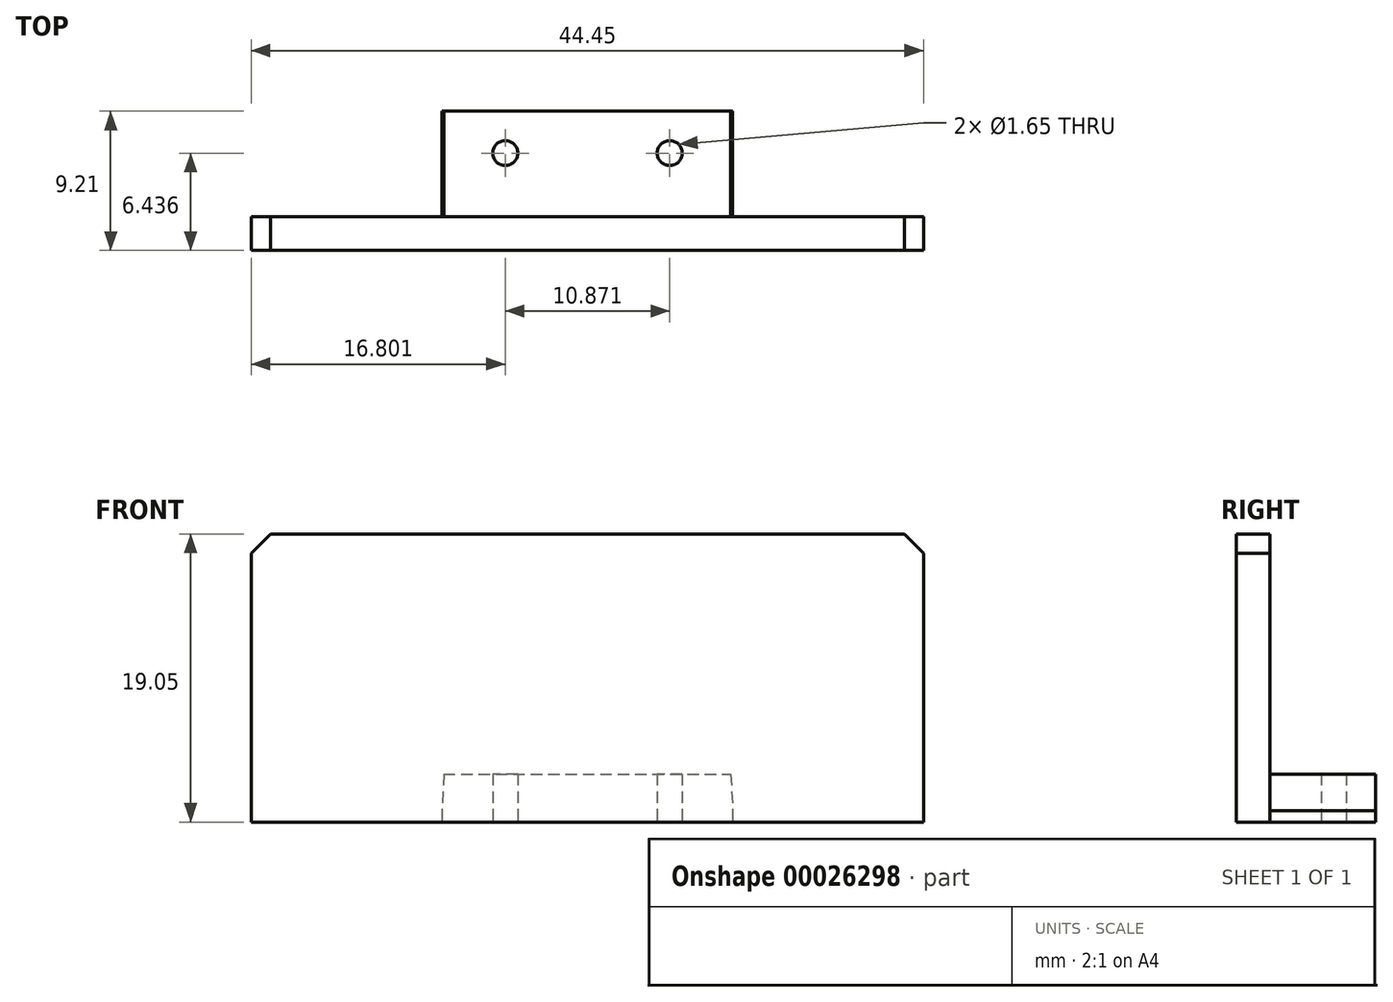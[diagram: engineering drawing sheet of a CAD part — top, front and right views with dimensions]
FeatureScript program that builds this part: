
annotation { "Feature Type Name" : "Feature", "Feature Type Description" : "" }
export const myFeature = defineFeature(function(context is Context, id is Id, definition is map)
    precondition{}
    {
        {
            var Q0;
            Q0=qCreatedBy(makeId("Top.planeOp"),FACE);
            var sketch = newSketch(context, id + "F0", { "sketchPlane" : qUnion([Q0])});
            skLineSegment(sketch, "E0.bottom", {"start": v(0, 0) * mm, "end": v(19.23, 0) * mm});
            skLineSegment(sketch, "E0.top", {"start": v(0, 6.99) * mm, "end": v(19.23, 6.99) * mm});
            skLineSegment(sketch, "E0.left", {"start": v(0, 0) * mm, "end": v(0, 6.99) * mm});
            skLineSegment(sketch, "E0.right", {"start": v(19.23, 0) * mm, "end": v(19.23, 6.99) * mm});
            skLineSegment(sketch, "E1", {"start": v(9.61, 6.99) * mm, "end": v(9.61, 0) * mm, "construction": true});
            skSolve(sketch);
        }
        {
            var Q0;
            Q0=makeQuery(id+"F0.imprint","IMPRINT",FACE,{"disambiguationData":[TD([[makeQuery(id+"F0.imprint","IMPRINT",EDGE,{"derivedFrom":sQuery(id+"F0.wireOp",EDGE,"E0.bottom")}),1.0]])]});
            extrude(context, id + "F1", {"entities" : qUnion([Q0]), "depth" : 3.17 * mm});
        }
        {
            var Q0;
            Q0=makeQuery(id+"F1.opExtrude","CAP_FACE",FACE,{"disambiguationData":[OSD([sQuery(id+"F0.wireOp",EDGE,"E0.bottom"),sQuery(id+"F0.wireOp",EDGE,"E0.top"),sQuery(id+"F0.wireOp",EDGE,"E0.left"),sQuery(id+"F0.wireOp",EDGE,"E0.right")])],"isStart":false});
            var sketch = newSketch(context, id + "F2", { "sketchPlane" : qUnion([Q0])});
            skCircle(sketch, "E2", {"center": v(4.2, 4.22) * mm, "radius": 1.71 * mm});
            skSolve(sketch);
        }
        {
            var Q0;
            Q0=makeQuery(id+"F2.imprint","IMPRINT",FACE,{"disambiguationData":[TD([[makeQuery(id+"F2.imprint","IMPRINT",EDGE,{"derivedFrom":sQuery(id+"F2.wireOp",EDGE,"E2")}),-1.0]])]});
            cPlane(context, id + "F3", {"entities" : qUnion([Q0]), "cplaneType" : CPlaneType.OFFSET, "offset" : 0.84 * mm, "width" : 152.4 * mm, "height" : 152.4 * mm});
        }
        {
            var Q0;
            Q0=qCreatedBy(id+"F3.planeOp",FACE);
            var sketch = newSketch(context, id + "F4", { "sketchPlane" : qUnion([Q0])});
            skCircle(sketch, "E3", {"center": v(4.2, 4.22) * mm, "radius": 1.52 * mm});
            skSolve(sketch);
        }
        {
            var Q0;
            Q0=makeQuery(id+"F1.opExtrude","CAP_FACE",FACE,{"disambiguationData":[OSD([sQuery(id+"F0.wireOp",EDGE,"E0.bottom"),sQuery(id+"F0.wireOp",EDGE,"E0.top"),sQuery(id+"F0.wireOp",EDGE,"E0.left"),sQuery(id+"F0.wireOp",EDGE,"E0.right")])],"isStart":false});
            var sketch = newSketch(context, id + "F5", { "sketchPlane" : qUnion([Q0])});
            skCircle(sketch, "E4", {"center": v(15.06, 4.22) * mm, "radius": 1.71 * mm});
            skSolve(sketch);
        }
        {
            var Q0;
            Q0=qCreatedBy(id+"F3.planeOp",FACE);
            var sketch = newSketch(context, id + "F6", { "sketchPlane" : qUnion([Q0])});
            skCircle(sketch, "E5", {"center": v(15.06, 4.22) * mm, "radius": 1.52 * mm});
            skSolve(sketch);
        }
        {
            var Q0;
            Q0=makeQuery(id+"F1.opExtrude","CAP_FACE",FACE,{"disambiguationData":[OSD([sQuery(id+"F0.wireOp",EDGE,"E0.bottom"),sQuery(id+"F0.wireOp",EDGE,"E0.top"),sQuery(id+"F0.wireOp",EDGE,"E0.left"),sQuery(id+"F0.wireOp",EDGE,"E0.right")])],"isStart":true});
            var sketch = newSketch(context, id + "F7", { "sketchPlane" : qUnion([Q0])});
            skLineSegment(sketch, "E6.bottom", {"start": v(-12.61, 2.22) * mm, "end": v(31.84, 2.22) * mm});
            skLineSegment(sketch, "E6.top", {"start": v(-12.61, 0) * mm, "end": v(31.84, 0) * mm});
            skLineSegment(sketch, "E6.left", {"start": v(-12.61, 2.22) * mm, "end": v(-12.61, 0) * mm});
            skLineSegment(sketch, "E6.right", {"start": v(31.84, 2.22) * mm, "end": v(31.84, 0) * mm});
            skPoint(sketch, "E7", {"position": v(9.61, 0) * mm});
            skSolve(sketch);
        }
        {
            var Q0;
            Q0=makeQuery(id+"F7.imprint","IMPRINT",FACE,{"disambiguationData":[TD([[makeQuery(id+"F7.imprint","IMPRINT",EDGE,{"derivedFrom":sQuery(id+"F7.wireOp",EDGE,"E6.bottom")}),-1.0]])]});
            extrude(context, id + "F8", {"entities" : qUnion([Q0]), "operationType" : NewBodyOperationType.ADD, "oppositeDirection" : true, "depth" : 19.05 * mm});
        }
        {
            var Q0;
            Q0=makeQuery(id+"F0.imprint","IMPRINT",FACE,{"disambiguationData":[TD([[makeQuery(id+"F0.imprint","IMPRINT",EDGE,{"derivedFrom":sQuery(id+"F0.wireOp",EDGE,"E0.bottom")}),1.0]])]});
            var sketch = newSketch(context, id + "F9", { "sketchPlane" : qUnion([Q0])});
            skCircle(sketch, "E8", {"center": v(4.2, 4.22) * mm, "radius": 0.83 * mm});
            skCircle(sketch, "E9", {"center": v(15.06, 4.22) * mm, "radius": 0.83 * mm});
            skSolve(sketch);
        }
        {
            var Q0;
            Q0 = qSketchRegion(id + "F9", true);
            extrude(context, id + "F10", {"entities" : qUnion([Q0]), "operationType" : NewBodyOperationType.REMOVE, "endBound" : BoundingType.THROUGH_ALL, "depth" : 25.4 * mm});
        }
        {
            var Q0;
            Q0=makeQuery(id+"F8.opExtrude","CAP_EDGE",EDGE,{"disambiguationData":[OSD([sQuery(id+"F7.wireOp",EDGE,"E6.left")])],"isStart":false});
            var Q1;
            Q1=makeQuery(id+"F8.opExtrude","CAP_EDGE",EDGE,{"disambiguationData":[OSD([sQuery(id+"F7.wireOp",EDGE,"E6.right")])],"isStart":false});
            chamfer(context, id + "F11", {"entities" : qUnion([Q0, Q1]), "width" : 1.27 * mm});
        }
        {
            var Q0;
            Q0=makeQuery(id+"F1.opExtrude","CAP_EDGE",EDGE,{"disambiguationData":[OSD([sQuery(id+"F0.wireOp",EDGE,"E0.right")])],"isStart":false});
            var Q1;
            Q1=makeQuery(id+"F1.opExtrude","CAP_EDGE",EDGE,{"disambiguationData":[OSD([sQuery(id+"F0.wireOp",EDGE,"E0.left")])],"isStart":false});
            chamfer(context, id + "F12", {"entities" : qUnion([Q0, Q1]), "chamferType" : ChamferType.OFFSET_ANGLE, "width" : 0.13 * mm, "oppositeDirection" : false, "angle" : 87 * degree});
        }
    });
